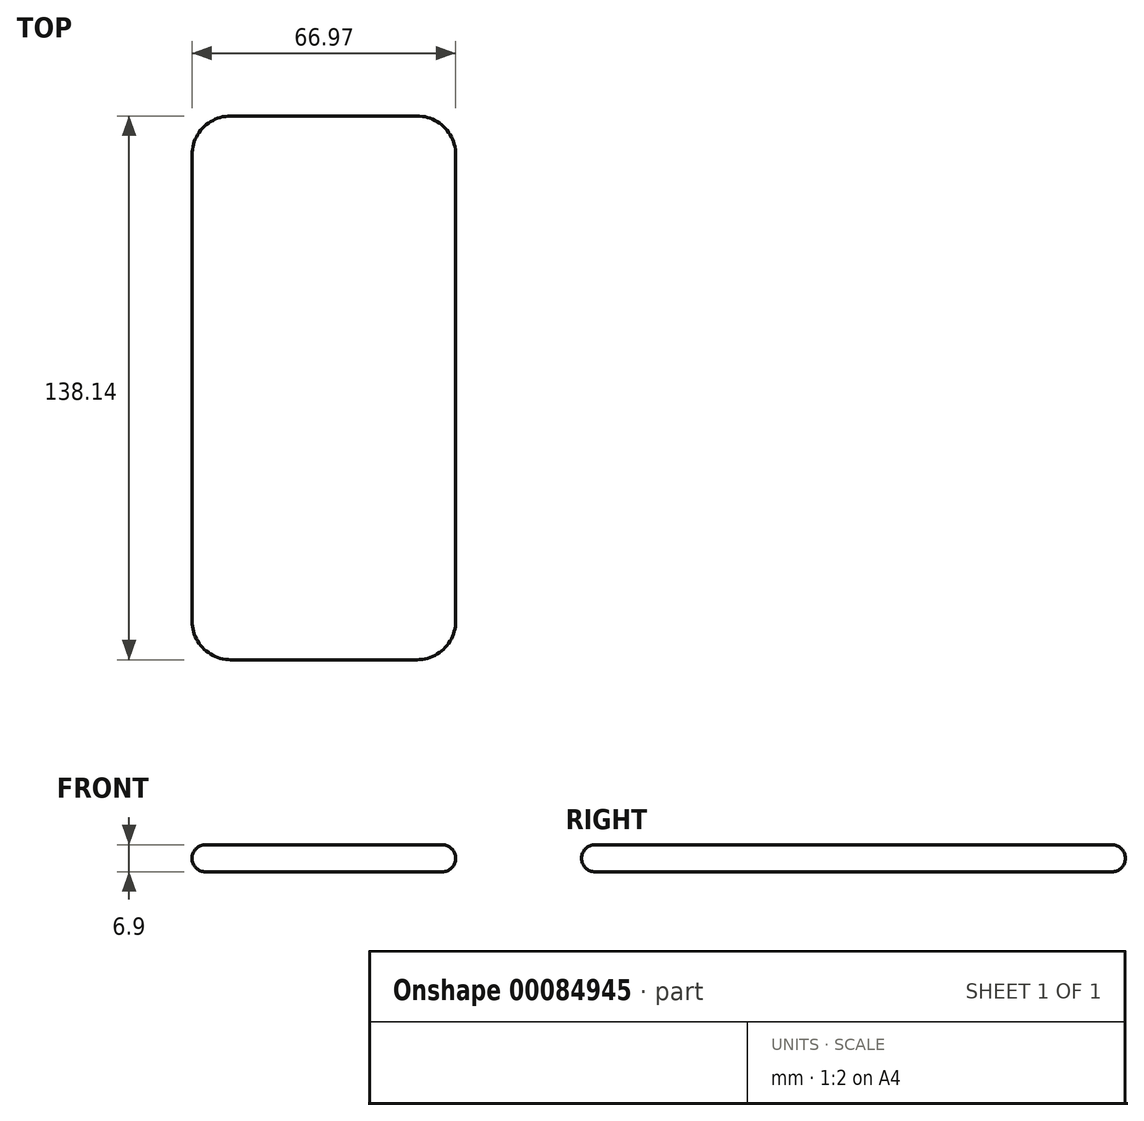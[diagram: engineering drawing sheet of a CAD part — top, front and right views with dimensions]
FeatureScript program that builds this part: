
annotation { "Feature Type Name" : "Feature", "Feature Type Description" : "" }
export const myFeature = defineFeature(function(context is Context, id is Id, definition is map)
    precondition{}
    {
        {
            var Q0;
            Q0=qCreatedBy(makeId("Front.planeOp"),FACE);
            var sketch = newSketch(context, id + "F0", { "sketchPlane" : qUnion([Q0])});
            skLineSegment(sketch, "E0.bottom", {"start": v(-33.48, -0.1) * mm, "end": v(33.48, -0.1) * mm});
            skLineSegment(sketch, "E0.top", {"start": v(-33.49, 6.8) * mm, "end": v(33.48, 6.8) * mm});
            skLineSegment(sketch, "E0.left", {"start": v(-33.48, -0.1) * mm, "end": v(-33.48, 6.8) * mm});
            skLineSegment(sketch, "E0.right", {"start": v(33.48, -0.1) * mm, "end": v(33.48, 6.8) * mm});
            skSolve(sketch);
        }
        {
            var Q0;
            Q0=makeQuery(id+"F0.imprint","IMPRINT",FACE,{"disambiguationData":[TD([[makeQuery(id+"F0.imprint","IMPRINT",EDGE,{"derivedFrom":sQuery(id+"F0.wireOp",EDGE,"E0.bottom")}),1.0]])]});
            extrude(context, id + "F1", {"entities" : qUnion([Q0]), "depth" : 138.14 * mm});
        }
        {
            var Q0;
            Q0=makeQuery(id+"F1.opExtrude","CAP_EDGE",EDGE,{"disambiguationData":[OSD([sQuery(id+"F0.wireOp",EDGE,"E0.left")])],"isStart":false});
            var Q1;
            Q1=makeQuery(id+"F1.opExtrude","CAP_EDGE",EDGE,{"disambiguationData":[OSD([sQuery(id+"F0.wireOp",EDGE,"E0.right")])],"isStart":false});
            var Q2;
            Q2=makeQuery(id+"F1.opExtrude","CAP_EDGE",EDGE,{"disambiguationData":[OSD([sQuery(id+"F0.wireOp",EDGE,"E0.right")])],"isStart":true});
            var Q3;
            Q3=makeQuery(id+"F1.opExtrude","CAP_EDGE",EDGE,{"disambiguationData":[OSD([sQuery(id+"F0.wireOp",EDGE,"E0.left")])],"isStart":true});
            fillet(context, id + "F2", {"entities" : qUnion([Q0, Q1, Q2, Q3]), "radius" : 9.8 * mm, "tangentPropagation" : true, "allowEdgeOverflow" : false});
        }
        {
            var Q0;
            Q0=makeQuery(id+"F1.opExtrude","SWEPT_EDGE",EDGE,{"disambiguationData":[OSD([sQuery(id+"F0.wireOp",EDGE,"E0.top"),sQuery(id+"F0.wireOp",EDGE,"E0.right")])]});
            var Q1;
            Q1=makeQuery(id+"F2.opFillet","BLEND_EDGE",EDGE,{"blendedFrom":[makeQuery(id+"F1.opExtrude","CAP_EDGE",EDGE,{"disambiguationData":[OSD([sQuery(id+"F0.wireOp",EDGE,"E0.right")])],"isStart":false}),makeQuery(id+"F1.opExtrude","SWEPT_FACE",FACE,{"disambiguationData":[OSD([sQuery(id+"F0.wireOp",EDGE,"E0.top")])]})],"blendedInto":[makeQuery(id+"F1.opExtrude","SWEPT_FACE",FACE,{"disambiguationData":[OSD([sQuery(id+"F0.wireOp",EDGE,"E0.top")])]})]});
            var Q2;
            Q2=makeQuery(id+"F1.opExtrude","CAP_EDGE",EDGE,{"disambiguationData":[OSD([sQuery(id+"F0.wireOp",EDGE,"E0.top")])],"isStart":false});
            var Q3;
            Q3=makeQuery(id+"F2.opFillet","BLEND_EDGE",EDGE,{"blendedFrom":[makeQuery(id+"F1.opExtrude","CAP_EDGE",EDGE,{"disambiguationData":[OSD([sQuery(id+"F0.wireOp",EDGE,"E0.left")])],"isStart":false}),makeQuery(id+"F1.opExtrude","SWEPT_FACE",FACE,{"disambiguationData":[OSD([sQuery(id+"F0.wireOp",EDGE,"E0.top")])]})],"blendedInto":[makeQuery(id+"F1.opExtrude","SWEPT_FACE",FACE,{"disambiguationData":[OSD([sQuery(id+"F0.wireOp",EDGE,"E0.top")])]})]});
            var Q4;
            Q4=makeQuery(id+"F1.opExtrude","SWEPT_EDGE",EDGE,{"disambiguationData":[OSD([sQuery(id+"F0.wireOp",EDGE,"E0.top"),sQuery(id+"F0.wireOp",EDGE,"E0.left")])]});
            var Q5;
            Q5=makeQuery(id+"F2.opFillet","BLEND_EDGE",EDGE,{"blendedFrom":[makeQuery(id+"F1.opExtrude","CAP_EDGE",EDGE,{"disambiguationData":[OSD([sQuery(id+"F0.wireOp",EDGE,"E0.left")])],"isStart":true}),makeQuery(id+"F1.opExtrude","SWEPT_FACE",FACE,{"disambiguationData":[OSD([sQuery(id+"F0.wireOp",EDGE,"E0.top")])]})],"blendedInto":[makeQuery(id+"F1.opExtrude","SWEPT_FACE",FACE,{"disambiguationData":[OSD([sQuery(id+"F0.wireOp",EDGE,"E0.top")])]})]});
            var Q6;
            Q6=makeQuery(id+"F1.opExtrude","CAP_EDGE",EDGE,{"disambiguationData":[OSD([sQuery(id+"F0.wireOp",EDGE,"E0.top")])],"isStart":true});
            var Q7;
            Q7=makeQuery(id+"F2.opFillet","BLEND_EDGE",EDGE,{"blendedFrom":[makeQuery(id+"F1.opExtrude","CAP_EDGE",EDGE,{"disambiguationData":[OSD([sQuery(id+"F0.wireOp",EDGE,"E0.right")])],"isStart":true}),makeQuery(id+"F1.opExtrude","SWEPT_FACE",FACE,{"disambiguationData":[OSD([sQuery(id+"F0.wireOp",EDGE,"E0.top")])]})],"blendedInto":[makeQuery(id+"F1.opExtrude","SWEPT_FACE",FACE,{"disambiguationData":[OSD([sQuery(id+"F0.wireOp",EDGE,"E0.top")])]})]});
            var Q8;
            Q8=makeQuery(id+"F2.opFillet","BLEND_EDGE",EDGE,{"blendedFrom":[makeQuery(id+"F1.opExtrude","CAP_EDGE",EDGE,{"disambiguationData":[OSD([sQuery(id+"F0.wireOp",EDGE,"E0.right")])],"isStart":false}),makeQuery(id+"F1.opExtrude","SWEPT_FACE",FACE,{"disambiguationData":[OSD([sQuery(id+"F0.wireOp",EDGE,"E0.bottom")])]})],"blendedInto":[makeQuery(id+"F1.opExtrude","SWEPT_FACE",FACE,{"disambiguationData":[OSD([sQuery(id+"F0.wireOp",EDGE,"E0.bottom")])]})]});
            var Q9;
            Q9=makeQuery(id+"F1.opExtrude","SWEPT_EDGE",EDGE,{"disambiguationData":[OSD([sQuery(id+"F0.wireOp",EDGE,"E0.bottom"),sQuery(id+"F0.wireOp",EDGE,"E0.right")])]});
            var Q10;
            Q10=makeQuery(id+"F1.opExtrude","CAP_EDGE",EDGE,{"disambiguationData":[OSD([sQuery(id+"F0.wireOp",EDGE,"E0.bottom")])],"isStart":false});
            var Q11;
            Q11=makeQuery(id+"F2.opFillet","BLEND_EDGE",EDGE,{"blendedFrom":[makeQuery(id+"F1.opExtrude","CAP_EDGE",EDGE,{"disambiguationData":[OSD([sQuery(id+"F0.wireOp",EDGE,"E0.left")])],"isStart":false}),makeQuery(id+"F1.opExtrude","SWEPT_FACE",FACE,{"disambiguationData":[OSD([sQuery(id+"F0.wireOp",EDGE,"E0.bottom")])]})],"blendedInto":[makeQuery(id+"F1.opExtrude","SWEPT_FACE",FACE,{"disambiguationData":[OSD([sQuery(id+"F0.wireOp",EDGE,"E0.bottom")])]})]});
            var Q12;
            Q12=makeQuery(id+"F1.opExtrude","SWEPT_EDGE",EDGE,{"disambiguationData":[OSD([sQuery(id+"F0.wireOp",EDGE,"E0.bottom"),sQuery(id+"F0.wireOp",EDGE,"E0.left")])]});
            var Q13;
            Q13=makeQuery(id+"F2.opFillet","BLEND_EDGE",EDGE,{"blendedFrom":[makeQuery(id+"F1.opExtrude","CAP_EDGE",EDGE,{"disambiguationData":[OSD([sQuery(id+"F0.wireOp",EDGE,"E0.left")])],"isStart":true}),makeQuery(id+"F1.opExtrude","SWEPT_FACE",FACE,{"disambiguationData":[OSD([sQuery(id+"F0.wireOp",EDGE,"E0.bottom")])]})],"blendedInto":[makeQuery(id+"F1.opExtrude","SWEPT_FACE",FACE,{"disambiguationData":[OSD([sQuery(id+"F0.wireOp",EDGE,"E0.bottom")])]})]});
            var Q14;
            Q14=makeQuery(id+"F1.opExtrude","CAP_EDGE",EDGE,{"disambiguationData":[OSD([sQuery(id+"F0.wireOp",EDGE,"E0.bottom")])],"isStart":true});
            var Q15;
            Q15=makeQuery(id+"F2.opFillet","BLEND_EDGE",EDGE,{"blendedFrom":[makeQuery(id+"F1.opExtrude","CAP_EDGE",EDGE,{"disambiguationData":[OSD([sQuery(id+"F0.wireOp",EDGE,"E0.right")])],"isStart":true}),makeQuery(id+"F1.opExtrude","SWEPT_FACE",FACE,{"disambiguationData":[OSD([sQuery(id+"F0.wireOp",EDGE,"E0.bottom")])]})],"blendedInto":[makeQuery(id+"F1.opExtrude","SWEPT_FACE",FACE,{"disambiguationData":[OSD([sQuery(id+"F0.wireOp",EDGE,"E0.bottom")])]})]});
            fillet(context, id + "F3", {"entities" : qUnion([Q0, Q1, Q2, Q3, Q4, Q5, Q6, Q7, Q8, Q9, Q10, Q11, Q12, Q13, Q14, Q15]), "radius" : 3.45 * mm, "tangentPropagation" : true, "allowEdgeOverflow" : false});
        }
    });
